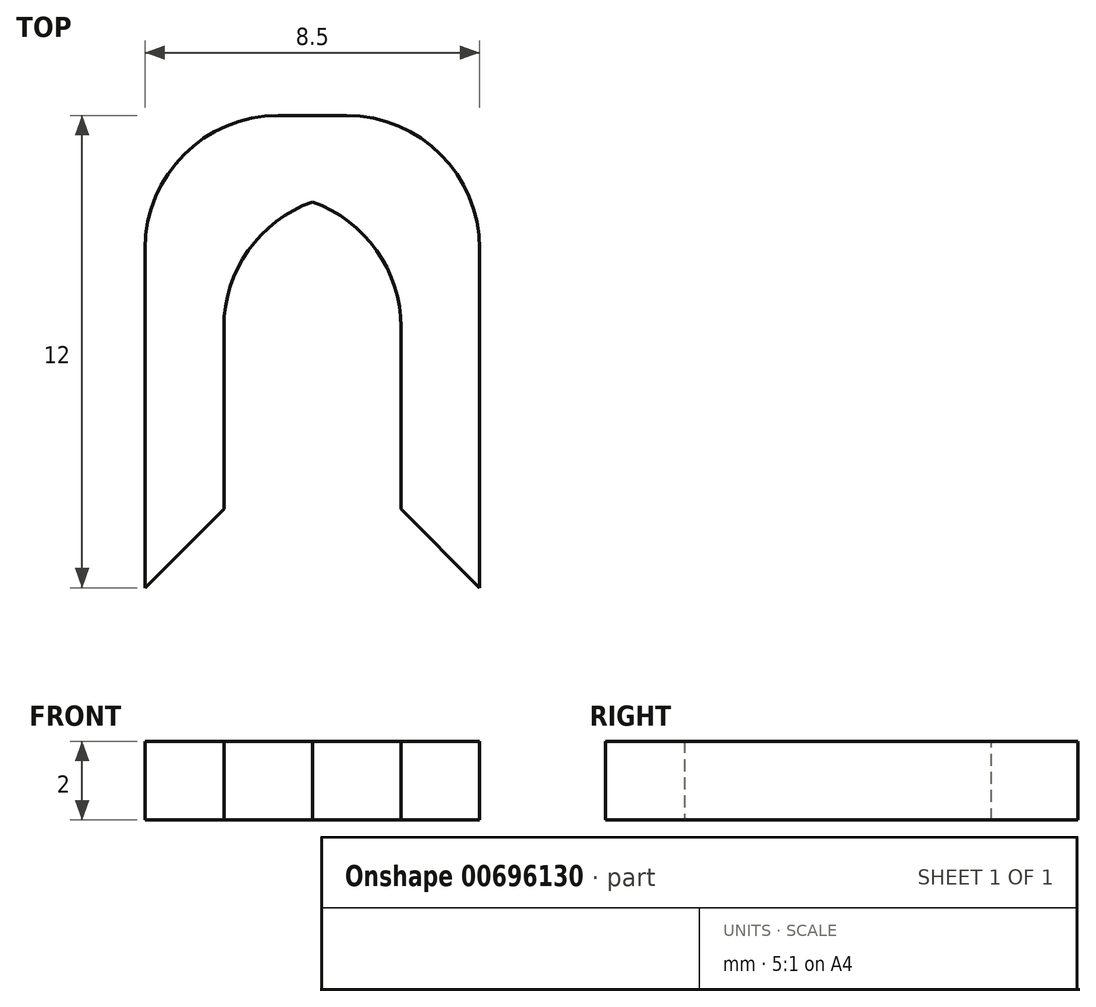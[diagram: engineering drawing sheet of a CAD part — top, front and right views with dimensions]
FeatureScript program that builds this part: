
annotation { "Feature Type Name" : "Feature", "Feature Type Description" : "" }
export const myFeature = defineFeature(function(context is Context, id is Id, definition is map)
    precondition{}
    {
        {
            var Q0;
            Q0=qCreatedBy(makeId("Top.planeOp"),FACE);
            var sketch = newSketch(context, id + "F0", { "sketchPlane" : qUnion([Q0])});
            skLineSegment(sketch, "E0.bottom", {"start": v(0, 0) * mm, "end": v(2, 0) * mm});
            skLineSegment(sketch, "E0.top", {"start": v(0, 12) * mm, "end": v(2, 12) * mm});
            skLineSegment(sketch, "E0.left", {"start": v(0, 0) * mm, "end": v(0, 12) * mm});
            skLineSegment(sketch, "E0.right", {"start": v(2, 0) * mm, "end": v(2, 12) * mm});
            skLineSegment(sketch, "E1.bottom", {"start": v(2, 12) * mm, "end": v(6.5, 12) * mm});
            skLineSegment(sketch, "E1.top", {"start": v(2, 10) * mm, "end": v(6.5, 10) * mm});
            skLineSegment(sketch, "E1.left", {"start": v(2, 12) * mm, "end": v(2, 10) * mm});
            skLineSegment(sketch, "E1.right", {"start": v(6.5, 12) * mm, "end": v(6.5, 10) * mm});
            skLineSegment(sketch, "E2.bottom", {"start": v(6.5, 12) * mm, "end": v(8.5, 12) * mm});
            skLineSegment(sketch, "E2.top", {"start": v(6.5, 0) * mm, "end": v(8.5, 0) * mm});
            skLineSegment(sketch, "E2.left", {"start": v(6.5, 12) * mm, "end": v(6.5, 0) * mm});
            skLineSegment(sketch, "E2.right", {"start": v(8.5, 12) * mm, "end": v(8.5, 0) * mm});
            skSolve(sketch);
        }
        {
            var Q0;
            Q0=makeQuery(id+"F0.imprint","IMPRINT",FACE,{"disambiguationData":[TD([[makeQuery(id+"F0.imprint","IMPRINT",EDGE,{"derivedFrom":sQuery(id+"F0.wireOp",EDGE,"E0.bottom")}),1.0]])]});
            var Q1;
            {var subQ3=sQuery(id+"F0.wireOp",EDGE,"E2.bottom");Q1=makeQuery(id+"F0.imprint","IMPRINT",FACE,{"disambiguationData":[TD([[makeQuery(id+"F0.imprint","IMPRINT",EDGE,{"derivedFrom":subQ3}),-1.0]])]});}
            var Q2;
            {var subQ0=sQuery(id+"F0.wireOp",EDGE,"E1.bottom");Q2=makeQuery(id+"F0.imprint","IMPRINT",FACE,{"disambiguationData":[TD([[makeQuery(id+"F0.imprint","IMPRINT",EDGE,{"derivedFrom":subQ0}),-1.0]])]});}
            extrude(context, id + "F1", {"entities" : qUnion([Q0, Q1, Q2]), "depth" : 2 * mm, "offsetDistance" : 25 * mm});
        }
        {
            var Q0;
            Q0=makeQuery(id+"F1.opExtrude","SWEPT_EDGE",EDGE,{"disambiguationData":[OSD([sQuery(id+"F0.wireOp",EDGE,"E0.top"),sQuery(id+"F0.wireOp",EDGE,"E0.left")])]});
            var Q1;
            Q1=makeQuery(id+"F1.opExtrude","SWEPT_EDGE",EDGE,{"disambiguationData":[OSD([sQuery(id+"F0.wireOp",EDGE,"E2.bottom"),sQuery(id+"F0.wireOp",EDGE,"E2.right")])]});
            var Q2;
            Q2=makeQuery(id+"F1.opExtrude","SWEPT_EDGE",EDGE,{"disambiguationData":[OSD([sQuery(id+"F0.wireOp",EDGE,"E1.top"),sQuery(id+"F0.wireOp",EDGE,"E2.left")])]});
            var Q3;
            Q3=makeQuery(id+"F1.opExtrude","SWEPT_EDGE",EDGE,{"disambiguationData":[OSD([sQuery(id+"F0.wireOp",EDGE,"E0.right"),sQuery(id+"F0.wireOp",EDGE,"E1.top"),sQuery(id+"F0.wireOp",EDGE,"E1.left")])]});
            fillet(context, id + "F2", {"entities" : qUnion([Q0, Q1, Q2, Q3]), "radius" : 3.38 * mm, "tangentPropagation" : true, "allowEdgeOverflow" : false});
        }
        {
            var Q0;
            Q0=makeQuery(id+"F1.opExtrude","SWEPT_EDGE",EDGE,{"disambiguationData":[OSD([sQuery(id+"F0.wireOp",EDGE,"E0.bottom"),sQuery(id+"F0.wireOp",EDGE,"E0.right")])]});
            var Q1;
            Q1=makeQuery(id+"F1.opExtrude","SWEPT_EDGE",EDGE,{"disambiguationData":[OSD([sQuery(id+"F0.wireOp",EDGE,"E2.top"),sQuery(id+"F0.wireOp",EDGE,"E2.left")])]});
            chamfer(context, id + "F3", {"entities" : qUnion([Q0, Q1]), "width" : 2 * mm, "tangentPropagation" : true});
        }
    });
